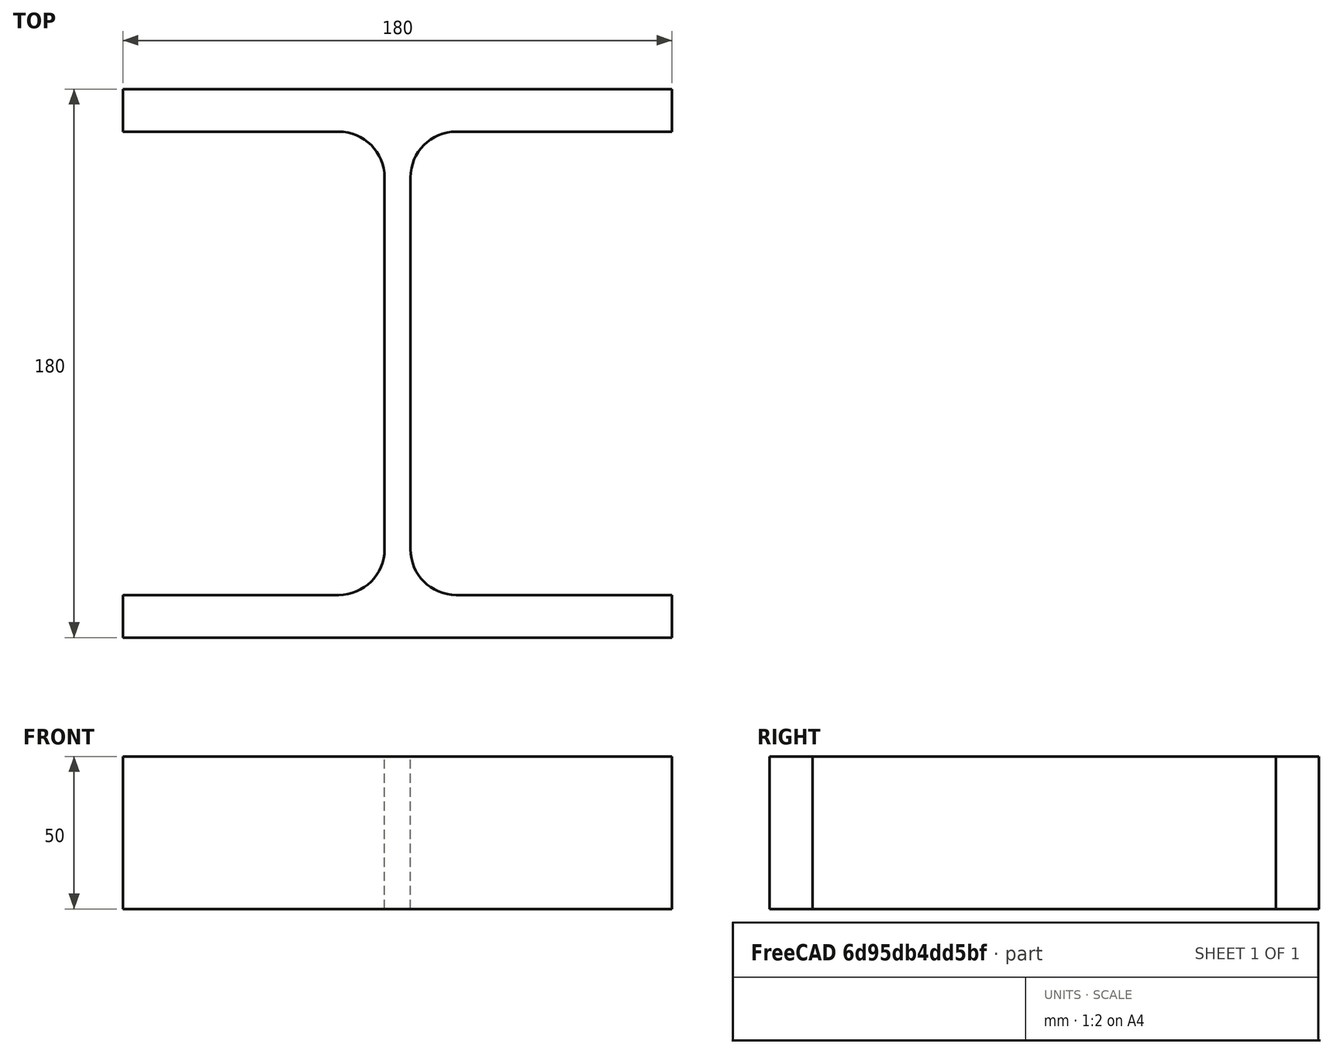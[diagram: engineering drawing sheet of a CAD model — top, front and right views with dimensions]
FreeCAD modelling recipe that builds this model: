
FCSTD DOCUMENT  (FreeCAD 0.15R4671 (Git))
Label: HE-B-Profile 180 DIN1025-2 S235JR
License: All rights reserved
LicenseURL: http://en.wikipedia.org/wiki/All_rights_reserved
objects: Sketcher::SketchObject×1, Part::Extrusion×1
note: 2 computed .brp shape members not serialized (recipe doc carries the construction recipe); baked Part::Feature solids carry a one-line shape summary decoded from their .brp

FEATURE [Sketcher::SketchObject] Sketch
  sketch-geometry (16):
    g0: LineSegment StartX=4.25 StartY=-61 StartZ=0 EndX=4.25 EndY=61 EndZ=0
    g1: LineSegment StartX=19.25 StartY=76 StartZ=0 EndX=90 EndY=76 EndZ=0
    g2: LineSegment StartX=90 StartY=76 StartZ=0 EndX=90 EndY=90 EndZ=0
    g3: LineSegment StartX=90 StartY=90 StartZ=0 EndX=-90 EndY=90 EndZ=0
    g4: LineSegment StartX=-90 StartY=90 StartZ=0 EndX=-90 EndY=76 EndZ=0
    g5: LineSegment StartX=-90 StartY=76 StartZ=0 EndX=-19.25 EndY=76 EndZ=0
    g6: LineSegment StartX=-4.25 StartY=61 StartZ=0 EndX=-4.25 EndY=-61 EndZ=0
    g7: LineSegment StartX=-19.25 StartY=-76 StartZ=0 EndX=-90 EndY=-76 EndZ=0
    g8: LineSegment StartX=-90 StartY=-76 StartZ=0 EndX=-90 EndY=-90 EndZ=0
    g9: LineSegment StartX=-90 StartY=-90 StartZ=0 EndX=90 EndY=-90 EndZ=0
    g10: LineSegment StartX=90 StartY=-90 StartZ=0 EndX=90 EndY=-76 EndZ=0
    g11: LineSegment StartX=90 StartY=-76 StartZ=0 EndX=19.25 EndY=-76 EndZ=0
    g12: ArcOfCircle CenterX=19.25 CenterY=61 CenterZ=0 NormalX=0 NormalY=0 NormalZ=1 Radius=15 StartAngle=1.5708 EndAngle=3.14159
    g13: ArcOfCircle CenterX=19.25 CenterY=-61 CenterZ=0 NormalX=0 NormalY=0 NormalZ=1 Radius=15 StartAngle=3.14159 EndAngle=4.71239
    g14: ArcOfCircle CenterX=-19.25 CenterY=61 CenterZ=0 NormalX=0 NormalY=0 NormalZ=1 Radius=15 StartAngle=0 EndAngle=1.5708
    g15: ArcOfCircle CenterX=-19.25 CenterY=-61 CenterZ=0 NormalX=0 NormalY=0 NormalZ=1 Radius=15 StartAngle=4.71239 EndAngle=6.28319
  constraints (42):
    c: Vertical(g0)
    c: Coincident(g2,g1)
    c: Vertical(g2)
    c: Coincident(g3,g2)
    c: Coincident(g4,g3)
    c: Vertical(g4)
    c: Coincident(g5,g4)
    c: Horizontal(g5)
    c: Vertical(g6)
    c: Horizontal(g7)
    c: Coincident(g8,g7)
    c: Vertical(g8)
    c: Coincident(g9,g8)
    c: Horizontal(g9)
    c: Coincident(g10,g9)
    c: Vertical(g10)
    c: Coincident(g11,g10)
    c: Horizontal(g11)
    c: Tangent(g1,g12) = 1.5708
    c: Tangent(g0,g12) = 1.5708
    c: Tangent(g0,g13) = 1.5708
    c: Tangent(g11,g13) = 1.5708
    c: Tangent(g5,g14) = 1.5708
    c: Tangent(g6,g14) = 1.5708
    c: Tangent(g6,g15) = 1.5708
    c: Tangent(g7,g15) = 1.5708
    c: Equal(g3,g9)
    c: Equal(g2,g4)
    c: Equal(g4,g8)
    c: Equal(g8,g10)
    c: Equal(g12,g14)
    c: Equal(g14,g15)
    c: Equal(g15,g13)
    c: Symmetric(g2,g3,g-2)
    c: Symmetric(g9,g8,g-2)
    c: Symmetric(g0,g6,g-2)
    c: Symmetric(g2,g9,g-1)
    c: DistanceY(g2,g9) = -180
    c: DistanceX(g3) = -180
    c: DistanceX(g0,g6) = -8.5
    c: DistanceY(g2) = 14
    c: Radius(g12) = 15
FEATURE [Part::Extrusion] Extrude  label="HE-B-Profile 180 DIN1025-2 S235JR"
  Base = -> Sketch
  Dir = (0,0,50)
  Solid = true
